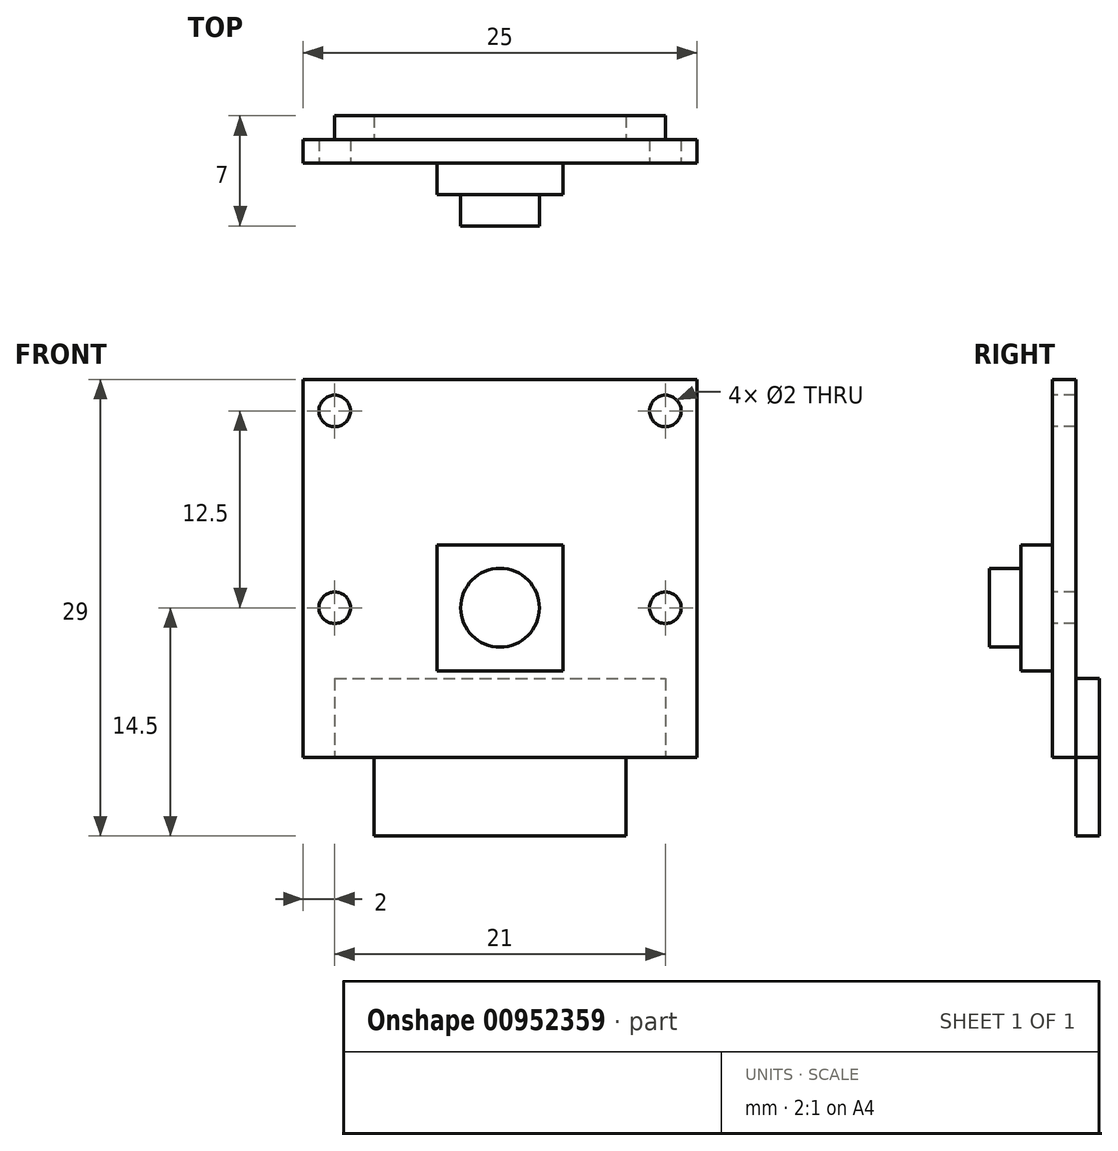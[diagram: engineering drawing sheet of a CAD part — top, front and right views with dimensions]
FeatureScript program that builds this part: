
annotation { "Feature Type Name" : "Feature", "Feature Type Description" : "" }
export const myFeature = defineFeature(function(context is Context, id is Id, definition is map)
    precondition{}
    {
        {
            var Q0;
            Q0=qCreatedBy(makeId("Front.planeOp"),FACE);
            var sketch = newSketch(context, id + "F0", { "sketchPlane" : qUnion([Q0])});
            skLineSegment(sketch, "E0.bottom", {"start": v(0, 0) * mm, "end": v(25, 0) * mm});
            skLineSegment(sketch, "E0.top", {"start": v(0, 24) * mm, "end": v(25, 24) * mm});
            skLineSegment(sketch, "E0.left", {"start": v(0, 0) * mm, "end": v(0, 24) * mm});
            skLineSegment(sketch, "E0.right", {"start": v(25, 0) * mm, "end": v(25, 24) * mm});
            skSolve(sketch);
        }
        {
            var Q0;
            Q0 = qSketchRegion(id + "F0", true);
            extrude(context, id + "F1", {"entities" : qUnion([Q0]), "depth" : 1.5 * mm, "offsetDistance" : 25 * mm});
        }
        {
            var Q0;
            Q0=makeQuery(id+"F1.opExtrude","CAP_FACE",FACE,{"disambiguationData":[OSD([sQuery(id+"F0.wireOp",EDGE,"E0.bottom"),sQuery(id+"F0.wireOp",EDGE,"E0.top"),sQuery(id+"F0.wireOp",EDGE,"E0.left"),sQuery(id+"F0.wireOp",EDGE,"E0.right")])],"isStart":false});
            var sketch = newSketch(context, id + "F2", { "sketchPlane" : qUnion([Q0])});
            skCircle(sketch, "E1", {"center": v(2, 22) * mm, "radius": 1 * mm});
            skCircle(sketch, "E2.0.1.0", {"center": v(2, 9.5) * mm, "radius": 1 * mm});
            skCircle(sketch, "E2.1.0.0", {"center": v(23, 22) * mm, "radius": 1 * mm});
            skCircle(sketch, "E2.1.1.0", {"center": v(23, 9.5) * mm, "radius": 1 * mm});
            skLineSegment(sketch, "E2.direction1", {"start": v(2, 22) * mm, "end": v(23, 22) * mm, "construction": true});
            skLineSegment(sketch, "E2.direction2", {"start": v(2, 22) * mm, "end": v(2, 9.5) * mm, "construction": true});
            skSolve(sketch);
        }
        {
            var Q0;
            Q0 = qSketchRegion(id + "F2", true);
            extrude(context, id + "F3", {"entities" : qUnion([Q0]), "operationType" : NewBodyOperationType.REMOVE, "endBound" : BoundingType.THROUGH_ALL, "oppositeDirection" : true, "depth" : 25 * mm, "offsetDistance" : 25 * mm});
        }
        {
            var Q0;
            Q0=makeQuery(id+"F1.opExtrude","CAP_FACE",FACE,{"disambiguationData":[OSD([sQuery(id+"F0.wireOp",EDGE,"E0.bottom"),sQuery(id+"F0.wireOp",EDGE,"E0.top"),sQuery(id+"F0.wireOp",EDGE,"E0.left"),sQuery(id+"F0.wireOp",EDGE,"E0.right")])],"isStart":false});
            var sketch = newSketch(context, id + "F4", { "sketchPlane" : qUnion([Q0])});
            skLineSegment(sketch, "E3.bottom", {"start": v(16.5, 13.5) * mm, "end": v(8.5, 13.5) * mm});
            skLineSegment(sketch, "E3.top", {"start": v(16.5, 5.5) * mm, "end": v(8.5, 5.5) * mm});
            skLineSegment(sketch, "E3.left", {"start": v(16.5, 13.5) * mm, "end": v(16.5, 5.5) * mm});
            skLineSegment(sketch, "E3.right", {"start": v(8.5, 13.5) * mm, "end": v(8.5, 5.5) * mm});
            skPoint(sketch, "E3.middle", {"position": v(12.5, 9.5) * mm});
            skCircle(sketch, "E4", {"center": v(12.5, 9.5) * mm, "radius": 2.5 * mm});
            skSolve(sketch);
        }
        {
            var Q0;
            Q0=makeQuery(id+"F4.imprint","IMPRINT",FACE,{"disambiguationData":[TD([[makeQuery(id+"F4.imprint","IMPRINT",EDGE,{"derivedFrom":sQuery(id+"F4.wireOp",EDGE,"E3.bottom")}),1.0]])]});
            extrude(context, id + "F5", {"entities" : qUnion([Q0]), "operationType" : NewBodyOperationType.ADD, "depth" : 2 * mm, "offsetDistance" : 25 * mm});
        }
        {
            var Q0;
            Q0=makeQuery(id+"F5.boolean.opBoolean","SPLIT",FACE,{"disambiguationData":[TD([makeQuery(id+"F5.opExtrude","SWEPT_FACE",FACE,{"disambiguationData":[OSD([sQuery(id+"F4.wireOp",EDGE,"E4")])]})])],"derivedFrom":makeQuery(id+"F1.opExtrude","CAP_FACE",FACE,{"disambiguationData":[OSD([sQuery(id+"F0.wireOp",EDGE,"E0.bottom"),sQuery(id+"F0.wireOp",EDGE,"E0.top"),sQuery(id+"F0.wireOp",EDGE,"E0.left"),sQuery(id+"F0.wireOp",EDGE,"E0.right")])],"isStart":false})});
            extrude(context, id + "F6", {"entities" : qUnion([Q0]), "operationType" : NewBodyOperationType.ADD, "depth" : 4 * mm, "offsetDistance" : 25 * mm});
        }
        {
            var Q0;
            Q0=makeQuery(id+"F1.opExtrude","CAP_FACE",FACE,{"disambiguationData":[OSD([sQuery(id+"F0.wireOp",EDGE,"E0.bottom"),sQuery(id+"F0.wireOp",EDGE,"E0.top"),sQuery(id+"F0.wireOp",EDGE,"E0.left"),sQuery(id+"F0.wireOp",EDGE,"E0.right")])],"isStart":true});
            var sketch = newSketch(context, id + "F7", { "sketchPlane" : qUnion([Q0])});
            skLineSegment(sketch, "E5.bottom", {"start": v(-2, 5) * mm, "end": v(-23, 5) * mm});
            skLineSegment(sketch, "E5.top", {"start": v(-4.5, -5) * mm, "end": v(-20.5, -5) * mm});
            skLineSegment(sketch, "E5.left", {"start": v(-2, 5) * mm, "end": v(-2, 0) * mm});
            skLineSegment(sketch, "E5.right", {"start": v(-23, 5) * mm, "end": v(-23, 0) * mm});
            skPoint(sketch, "E5.middle", {"position": v(-12.5, 0) * mm});
            skLineSegment(sketch, "E6", {"start": v(-23, 0) * mm, "end": v(-20.5, 0) * mm});
            skLineSegment(sketch, "E7", {"start": v(-20.5, 0) * mm, "end": v(-20.5, -5) * mm});
            skLineSegment(sketch, "E8", {"start": v(-12.5, 0) * mm, "end": v(-12.5, 24) * mm, "construction": true});
            skLineSegment(sketch, "E9.MirrorCS", {"start": v(-4.5, 0) * mm, "end": v(-4.5, -5) * mm});
            skLineSegment(sketch, "E10.MirrorCS", {"start": v(-2, 0) * mm, "end": v(-4.5, 0) * mm});
            skSolve(sketch);
        }
        {
            var Q0;
            Q0 = qSketchRegion(id + "F7", true);
            extrude(context, id + "F8", {"entities" : qUnion([Q0]), "operationType" : NewBodyOperationType.ADD, "depth" : 1.5 * mm, "offsetDistance" : 25 * mm});
        }
    });
